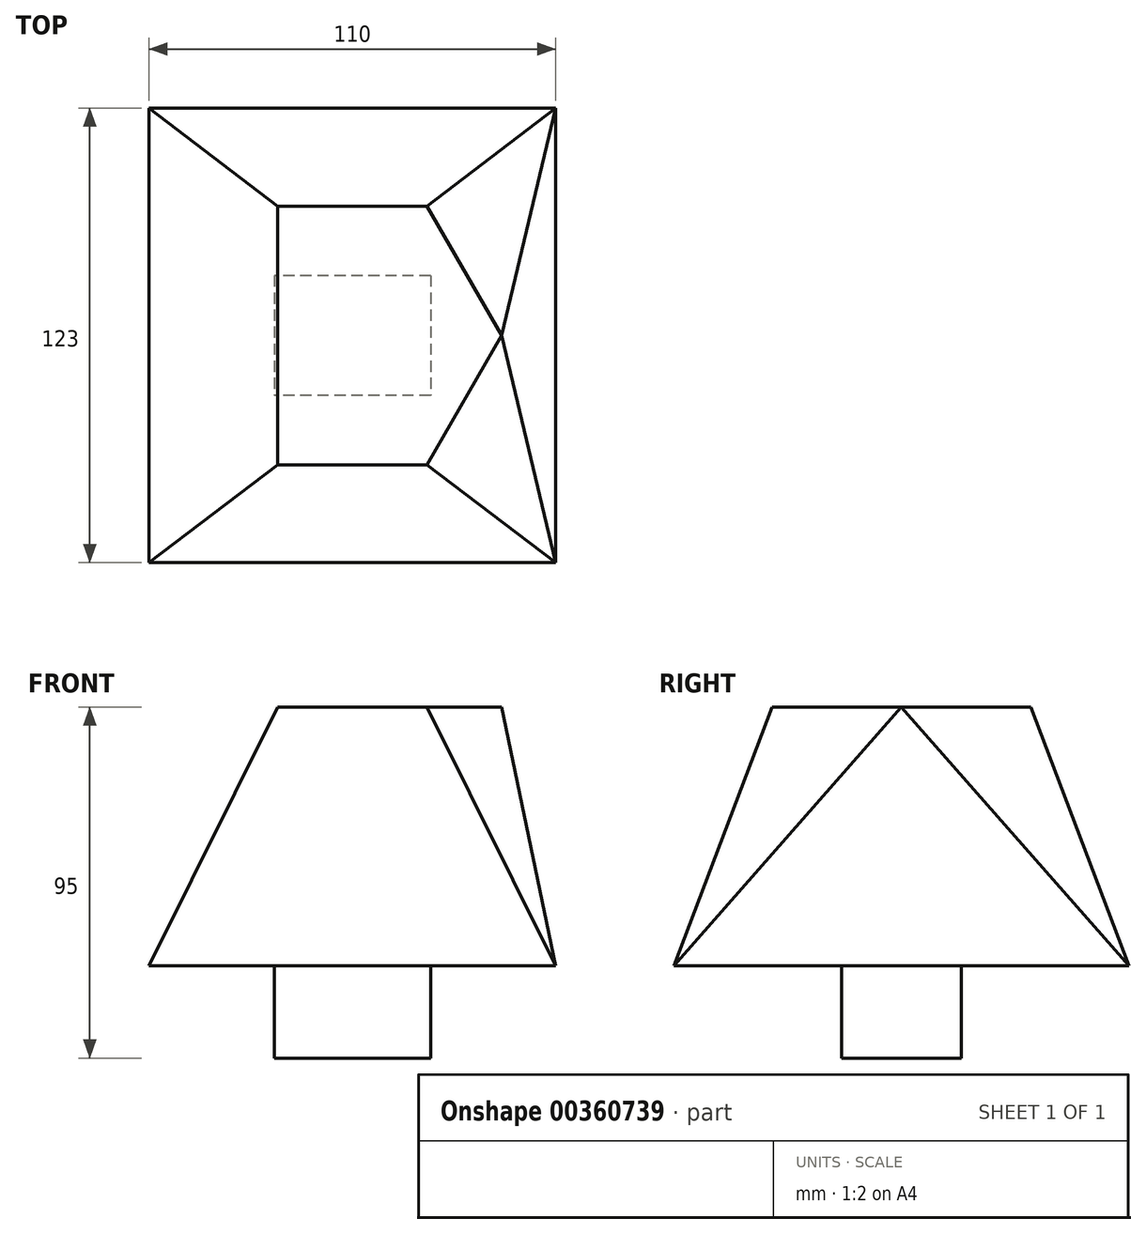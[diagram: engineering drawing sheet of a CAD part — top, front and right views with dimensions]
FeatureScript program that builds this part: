
annotation { "Feature Type Name" : "Feature", "Feature Type Description" : "" }
export const myFeature = defineFeature(function(context is Context, id is Id, definition is map)
    precondition{}
    {
        {
            var Q0;
            Q0=qCreatedBy(makeId("Top.planeOp"),FACE);
            var sketch = newSketch(context, id + "F0", { "sketchPlane" : qUnion([Q0])});
            skLineSegment(sketch, "E0.bottom", {"start": v(55, -61.5) * mm, "end": v(-55, -61.5) * mm});
            skLineSegment(sketch, "E0.top", {"start": v(55, 61.5) * mm, "end": v(-55, 61.5) * mm});
            skLineSegment(sketch, "E0.left", {"start": v(55, -61.5) * mm, "end": v(55, 61.5) * mm});
            skLineSegment(sketch, "E0.right", {"start": v(-55, -61.5) * mm, "end": v(-55, 61.5) * mm});
            skPoint(sketch, "E0.middle", {"position": v(0, 0) * mm});
            skSolve(sketch);
        }
        {
            var Q0;
            Q0=qCreatedBy(makeId("Top.planeOp"),FACE);
            cPlane(context, id + "F1", {"entities" : qUnion([Q0]), "cplaneType" : CPlaneType.OFFSET, "offset" : 70 * mm, "width" : 150 * mm, "height" : 150 * mm});
        }
        {
            var Q0;
            Q0=qCreatedBy(id+"F1.planeOp",FACE);
            var sketch = newSketch(context, id + "F2", { "sketchPlane" : qUnion([Q0])});
            skCircle(sketch, "E1.cCircle", {"center": v(0, 0) * mm, "radius": 40.41 * mm, "construction": true});
            skLineSegment(sketch, "E1.0", {"start": v(40.41, 0) * mm, "end": v(20.2, -35) * mm});
            skLineSegment(sketch, "E1.1", {"start": v(20.2, -35) * mm, "end": v(-20.2, -35) * mm});
            skLineSegment(sketch, "E1.2", {"start": v(-20.2, -35) * mm, "end": v(-40.41, 0) * mm});
            skLineSegment(sketch, "E1.3", {"start": v(-40.41, 0) * mm, "end": v(-20.2, 35) * mm});
            skLineSegment(sketch, "E1.4", {"start": v(-20.2, 35) * mm, "end": v(20.2, 35) * mm});
            skLineSegment(sketch, "E1.5", {"start": v(20.2, 35) * mm, "end": v(40.41, 0) * mm});
            skLineSegment(sketch, "E2", {"start": v(-20.2, 35) * mm, "end": v(-20.2, -35) * mm});
            skLineSegment(sketch, "E3", {"start": v(20.2, 35) * mm, "end": v(20.2, -35) * mm});
            skSolve(sketch);
        }
        {
            var Q0;
            Q0=makeQuery(id+"F2.imprint","IMPRINT",FACE,{"disambiguationData":[TD([[makeQuery(id+"F2.imprint","IMPRINT",EDGE,{"derivedFrom":sQuery(id+"F2.wireOp",EDGE,"E1.1")}),-1.0]])]});
            var Q1;
            Q1=makeQuery(id+"F0.imprint","IMPRINT",FACE,{"disambiguationData":[TD([[makeQuery(id+"F0.imprint","IMPRINT",EDGE,{"derivedFrom":sQuery(id+"F0.wireOp",EDGE,"E0.bottom")}),-1.0]])]});
            loft(context, id + "F3", {"sheetProfilesArray" : [{ "sheetProfileEntities" : qUnion([Q0]) }, { "sheetProfileEntities" : qUnion([Q1]) }]});
        }
        {
            var Q1;
            Q1=makeQuery(id+"F2.imprint","IMPRINT",FACE,{"disambiguationData":[TD([[makeQuery(id+"F2.imprint","IMPRINT",EDGE,{"derivedFrom":sQuery(id+"F2.wireOp",EDGE,"E1.0")}),-1.0]])]});
            var Q2;
            Q2=makeQuery(id+"F3.opLoft","MID_CAP_VERTEX",VERTEX,{"disambiguationData":[OSD([sQuery(id+"F0.wireOp",EDGE,"E0.bottom"),sQuery(id+"F0.wireOp",EDGE,"E0.left")])],"capPos":1.0});
            loft(context, id + "F4", {"operationType" : NewBodyOperationType.ADD, "sheetProfilesArray" : [{ "sheetProfileEntities" : qUnion([Q1]) }, { "sheetProfileEntities" : qUnion([Q2]) }]});
        }
        {
            var Q1;
            Q1=makeQuery(id+"F2.imprint","IMPRINT",FACE,{"disambiguationData":[TD([[makeQuery(id+"F2.imprint","IMPRINT",EDGE,{"derivedFrom":sQuery(id+"F2.wireOp",EDGE,"E1.0")}),-1.0]])]});
            var Q2;
            Q2=makeQuery(id+"F3.opLoft","MID_CAP_VERTEX",VERTEX,{"disambiguationData":[OSD([sQuery(id+"F0.wireOp",EDGE,"E0.top"),sQuery(id+"F0.wireOp",EDGE,"E0.left")])],"capPos":1.0});
            loft(context, id + "F5", {"operationType" : NewBodyOperationType.ADD, "sheetProfilesArray" : [{ "sheetProfileEntities" : qUnion([Q1]) }, { "sheetProfileEntities" : qUnion([Q2]) }]});
        }
        {
            var Q1;
            Q1=makeQuery(id+"F5.opLoft","SWEPT_FACE",FACE,{"disambiguationData":[OSD([sQuery(id+"F2.wireOp",EDGE,"E1.0"),sQuery(id+"F2.wireOp",EDGE,"E1.1"),sQuery(id+"F2.wireOp",EDGE,"E1.5"),sQuery(id+"F2.wireOp",EDGE,"E3")])]});
            var Q2;
            Q2=makeQuery(id+"F4.opLoft","SWEPT_FACE",FACE,{"disambiguationData":[OSD([sQuery(id+"F2.wireOp",EDGE,"E1.0"),sQuery(id+"F2.wireOp",EDGE,"E1.4"),sQuery(id+"F2.wireOp",EDGE,"E1.5"),sQuery(id+"F2.wireOp",EDGE,"E3")])]});
            var Q3;
            Q3=makeQuery(id+"F3.opLoft","MID_CAP_EDGE",EDGE,{"disambiguationData":[OSD([sQuery(id+"F0.wireOp",EDGE,"E0.bottom"),sQuery(id+"F0.wireOp",EDGE,"E0.top"),sQuery(id+"F0.wireOp",EDGE,"E0.left")])],"capPos":1.0});
            loft(context, id + "F6", {"operationType" : NewBodyOperationType.ADD, "addGuides" : true, "sheetProfilesArray" : [{ "sheetProfileEntities" : qUnion([Q1]) }, { "sheetProfileEntities" : qUnion([Q2]) }], "guidesArray" : [{ "guideEntities" : qUnion([Q3]), "guideDerivativeType" : LoftGuideDerivativeType.DEFAULT, "guideDerivativeMagnitude" : 1 }]});
        }
        {
            var Q0;
            Q0=makeQuery(id+"F0.imprint","IMPRINT",FACE,{"disambiguationData":[TD([[makeQuery(id+"F0.imprint","IMPRINT",EDGE,{"derivedFrom":sQuery(id+"F0.wireOp",EDGE,"E0.bottom")}),-1.0]])]});
            var sketch = newSketch(context, id + "F7", { "sketchPlane" : qUnion([Q0])});
            skLineSegment(sketch, "E4.bottom", {"start": v(21.15, 16.19) * mm, "end": v(-21.15, 16.19) * mm});
            skLineSegment(sketch, "E4.top", {"start": v(21.15, -16.19) * mm, "end": v(-21.15, -16.19) * mm});
            skLineSegment(sketch, "E4.left", {"start": v(21.15, 16.19) * mm, "end": v(21.15, -16.19) * mm});
            skLineSegment(sketch, "E4.right", {"start": v(-21.15, 16.19) * mm, "end": v(-21.15, -16.19) * mm});
            skPoint(sketch, "E4.middle", {"position": v(0, 0) * mm});
            skSolve(sketch);
        }
        {
            var Q0;
            Q0=makeQuery(id+"F7.imprint","IMPRINT",FACE,{"disambiguationData":[TD([[makeQuery(id+"F7.imprint","IMPRINT",EDGE,{"derivedFrom":sQuery(id+"F7.wireOp",EDGE,"E4.bottom")}),1.0]])]});
            extrude(context, id + "F8", {"entities" : qUnion([Q0]), "operationType" : NewBodyOperationType.ADD, "oppositeDirection" : true, "depth" : 25 * mm, "offsetDistance" : 25 * mm});
        }
    });
